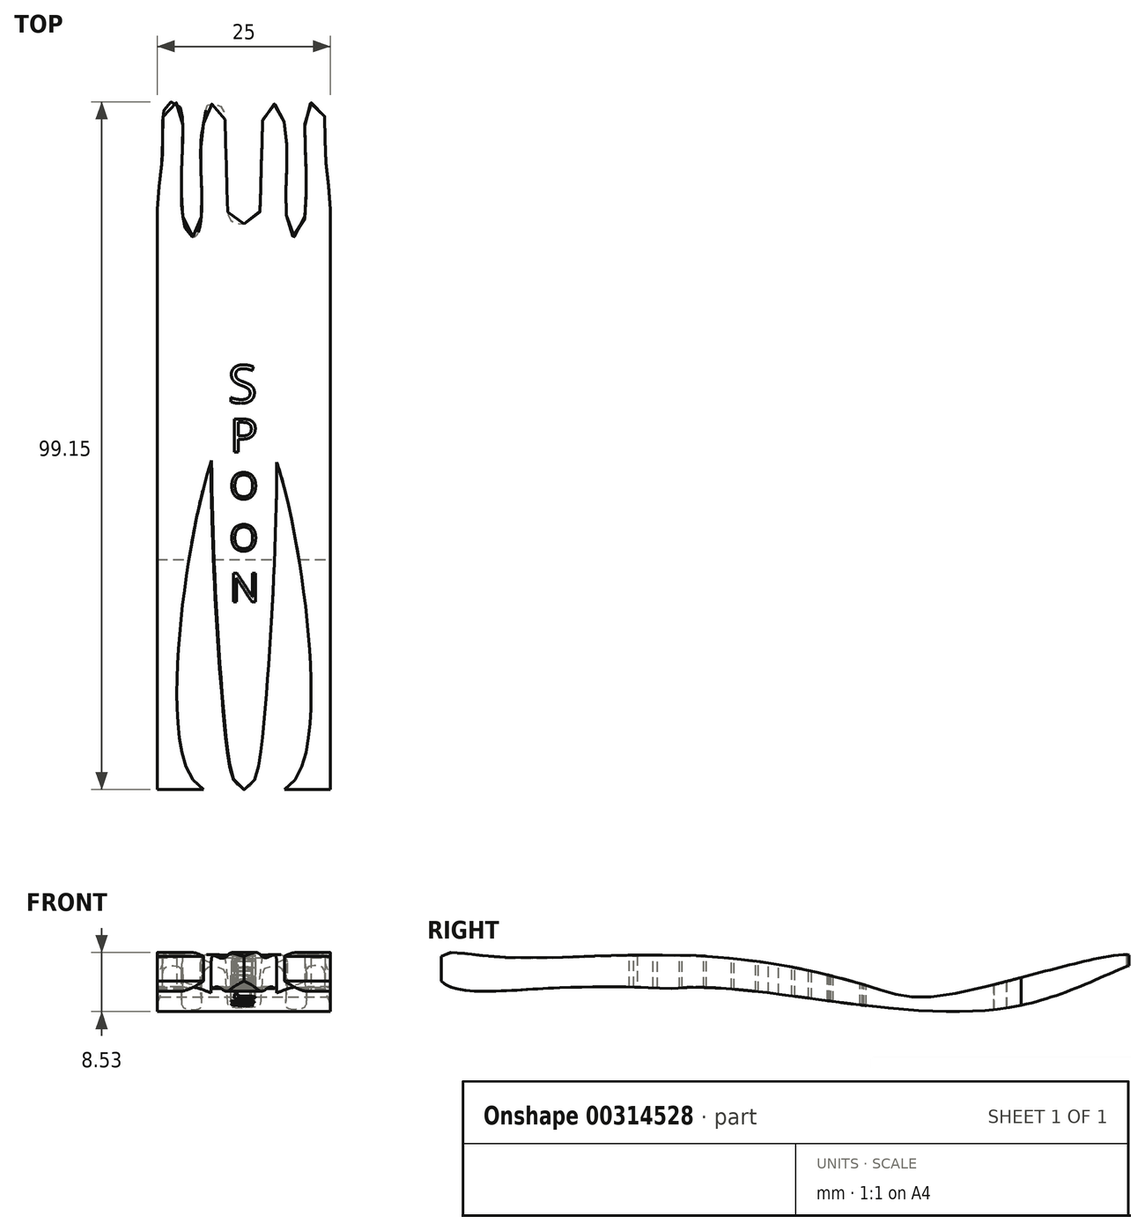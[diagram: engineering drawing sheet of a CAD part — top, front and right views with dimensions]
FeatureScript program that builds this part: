
annotation { "Feature Type Name" : "Feature", "Feature Type Description" : "" }
export const myFeature = defineFeature(function(context is Context, id is Id, definition is map)
    precondition{}
    {
        {
            var Q0;
            Q0=qCreatedBy(makeId("Top.planeOp"),FACE);
            var sketch = newSketch(context, id + "F0", { "sketchPlane" : qUnion([Q0])});
            skLineSegment(sketch, "E0.bottom", {"start": v(12.5, 50) * mm, "end": v(-12.5, 50) * mm});
            skLineSegment(sketch, "E0.top", {"start": v(12.5, -50) * mm, "end": v(-12.5, -50) * mm});
            skLineSegment(sketch, "E0.left", {"start": v(12.5, 50) * mm, "end": v(12.5, -50) * mm});
            skLineSegment(sketch, "E0.right", {"start": v(-12.5, 50) * mm, "end": v(-12.5, -50) * mm});
            skPoint(sketch, "E0.middle", {"position": v(0, 0) * mm});
            skSolve(sketch);
        }
        {
            var Q0;
            Q0=makeQuery(id+"F0.imprint","IMPRINT",FACE,{"disambiguationData":[TD([[makeQuery(id+"F0.imprint","IMPRINT",EDGE,{"derivedFrom":sQuery(id+"F0.wireOp",EDGE,"E0.bottom")}),1.0]])]});
            extrude(context, id + "F1", {"entities" : qUnion([Q0]), "depth" : 30 * mm});
        }
        {
            var Q0;
            Q0=makeQuery(id+"F1.opExtrude","CAP_FACE",FACE,{"disambiguationData":[OSD([sQuery(id+"F0.wireOp",EDGE,"E0.bottom"),sQuery(id+"F0.wireOp",EDGE,"E0.top"),sQuery(id+"F0.wireOp",EDGE,"E0.left"),sQuery(id+"F0.wireOp",EDGE,"E0.right")])],"isStart":false});
            var sketch = newSketch(context, id + "F2", { "sketchPlane" : qUnion([Q0])});
            skFitSpline(sketch, "E1.MirrorCS", {"points": [v(0, 31.54) * mm, v(-1.96, 32.06) * mm, v(-2.2, 32.35) * mm, v(-2.53, 40.64) * mm, v(-2.7, 45.52) * mm, v(-3.52, 48.65) * mm, v(-5.37, 48.65) * mm, v(-5.43, 48.53) * mm, v(-5.92, 45.53) * mm, v(-6.22, 40.95) * mm, v(-6.76, 29.96) * mm, v(-8.08, 30.17) * mm, v(-8.89, 41.38) * mm, v(-9.59, 48.9) * mm, v(-11.15, 48.73) * mm, v(-11.74, 41.56) * mm, v(-11.5, 27.74) * mm, v(-4.2, 21.83) * mm, v(-4.32, 9.89) * mm, v(-2.32, -45.14) * mm, v(0, -50) * mm, v(7.9, -47.77) * mm, v(3.4, 0.05) * mm, v(0.03, -49.28) * mm], "startDerivative": vector(-83.8, -22.38) * mm, "endDerivative": vector(1.6, -694.26) * mm});
            skLineSegment(sketch, "E2", {"start": v(0, 31.54) * mm, "end": v(0.03, -49.28) * mm});
            skFitSpline(sketch, "E3.MirrorCS", {"points": [v(0, 31.54) * mm, v(1.96, 32.06) * mm, v(2.2, 32.35) * mm, v(2.52, 40.65) * mm, v(2.69, 45.52) * mm, v(3.5, 48.65) * mm, v(5.35, 48.65) * mm, v(5.42, 48.53) * mm, v(5.91, 45.53) * mm, v(6.22, 40.95) * mm, v(6.77, 29.96) * mm, v(8.08, 30.17) * mm, v(8.88, 41.38) * mm, v(9.57, 48.9) * mm, v(11.14, 48.73) * mm, v(11.74, 41.57) * mm, v(11.5, 27.75) * mm, v(4.2, 21.83) * mm, v(4.33, 9.9) * mm, v(2.37, -45.14) * mm, v(0.05, -50) * mm, v(-7.84, -47.78) * mm, v(-3.37, 0.04) * mm, v(0.03, -49.28) * mm], "startDerivative": vector(83.82, -22.33) * mm, "endDerivative": vector(-1.16, -694.26) * mm});
            skSolve(sketch);
        }
        {
            var Q0;
            Q0=makeQuery(id+"F1.opExtrude","SWEPT_FACE",FACE,{"disambiguationData":[OSD([sQuery(id+"F0.wireOp",EDGE,"E0.left")])]});
            var sketch = newSketch(context, id + "F3", { "sketchPlane" : qUnion([Q0])});
            skLineSegment(sketch, "E4", {"start": v(0, 30) * mm, "end": v(0, 0) * mm, "construction": true});
            skLineSegment(sketch, "E5.bottom", {"start": v(50, 22.3) * mm, "end": v(-50, 22.3) * mm, "construction": true});
            skLineSegment(sketch, "E5.top", {"start": v(50, 7.7) * mm, "end": v(-50, 7.7) * mm, "construction": true});
            skLineSegment(sketch, "E5.left", {"start": v(50, 22.3) * mm, "end": v(50, 7.7) * mm, "construction": true});
            skLineSegment(sketch, "E5.right", {"start": v(-50, 22.3) * mm, "end": v(-50, 7.7) * mm, "construction": true});
            skPoint(sketch, "E5.middle", {"position": v(0, 15) * mm});
            skFitSpline(sketch, "E6", {"points": [v(50, 22.3) * mm, v(22.87, 16.73) * mm, v(12.16, 17.85) * mm, v(-11.49, 22.3) * mm, v(-43.17, 22.3) * mm, v(-50, 22.3) * mm, v(-50, 18.74) * mm, v(-36.03, 17.62) * mm, v(-12.83, 17.4) * mm, v(11.27, 14.05) * mm, v(22.42, 12.05) * mm, v(47.4, 18.3) * mm, v(50, 22.3) * mm]});
            skSolve(sketch);
        }
        {
            var Q0;
            {var subQ1=sQuery(id+"F0.wireOp",EDGE,"E0.left");var subQ6=makeQuery(id+"F1.opExtrude","CAP_EDGE",EDGE,{"disambiguationData":[OSD([subQ1])],"isStart":false});Q0=makeQuery(id+"F3.imprint","IMPRINT",FACE,{"disambiguationData":[TD([[makeQuery(id+"F3.imprint","IMPRINT",EDGE,{"derivedFrom":subQ6}),1.0]])]});}
            var Q1;
            {var subQ1=sQuery(id+"F0.wireOp",EDGE,"E0.left");var subQ6=makeQuery(id+"F1.opExtrude","CAP_EDGE",EDGE,{"disambiguationData":[OSD([subQ1])],"isStart":true});Q1=makeQuery(id+"F3.imprint","IMPRINT",FACE,{"disambiguationData":[TD([[makeQuery(id+"F3.imprint","IMPRINT",EDGE,{"derivedFrom":subQ6}),-1.0]])]});}
            extrude(context, id + "F4", {"entities" : qUnion([Q0, Q1]), "operationType" : NewBodyOperationType.REMOVE, "oppositeDirection" : true, "depth" : 30 * mm});
        }
        {
            var Q0;
            {var subQ0=sQuery(id+"F2.wireOp",EDGE,"E1.MirrorCS");var subQ1=makeQuery(id+"F1.opExtrude","CAP_EDGE",EDGE,{"disambiguationData":[OSD([sQuery(id+"F0.wireOp",EDGE,"E0.top")])],"isStart":false});var subQ2=makeQuery(id+"F2.imprint","INTERSECT",VERTEX,{"derivedFrom":[subQ1,subQ0]});Q0=makeQuery(id+"F2.imprint","IMPRINT",FACE,{"disambiguationData":[TD([[makeQuery(id+"F2.imprint","IMPRINT",EDGE,{"disambiguationData":[TD([[subQ2,1.0]])],"derivedFrom":subQ0}),-1.0]])]});}
            var Q1;
            {var subQ0=sQuery(id+"F2.wireOp",EDGE,"E3.MirrorCS");var subQ1=makeQuery(id+"F1.opExtrude","CAP_EDGE",EDGE,{"disambiguationData":[OSD([sQuery(id+"F0.wireOp",EDGE,"E0.top")])],"isStart":false});var subQ2=makeQuery(id+"F2.imprint","INTERSECT",VERTEX,{"derivedFrom":[subQ1,subQ0]});Q1=makeQuery(id+"F2.imprint","IMPRINT",FACE,{"disambiguationData":[TD([[makeQuery(id+"F2.imprint","IMPRINT",EDGE,{"disambiguationData":[TD([[subQ2,1.0]])],"derivedFrom":subQ0}),1.0]])]});}
            var Q2;
            {var subQ0=makeQuery(id+"F1.opExtrude","CAP_EDGE",EDGE,{"disambiguationData":[OSD([sQuery(id+"F0.wireOp",EDGE,"E0.bottom")])],"isStart":false});Q2=makeQuery(id+"F2.imprint","IMPRINT",FACE,{"disambiguationData":[TD([[makeQuery(id+"F2.imprint","IMPRINT",EDGE,{"derivedFrom":subQ0}),1.0]])]});}
            extrude(context, id + "F5", {"entities" : qUnion([Q0, Q1, Q2]), "operationType" : NewBodyOperationType.REMOVE, "oppositeDirection" : true, "depth" : 30 * mm});
        }
        {
            var Q0;
            Q0=qCreatedBy(makeId("Right.planeOp"),FACE);
            var sketch = newSketch(context, id + "F6", { "sketchPlane" : qUnion([Q0])});
            skFitSpline(sketch, "E7", {"points": [v(50.3, 21.42) * mm, v(35.14, 15.62) * mm, v(7.92, 15.62) * mm, v(-21.97, 15.4) * mm, v(7.7, -13.16) * mm, v(68.6, -10.26) * mm, v(58.11, 20.3) * mm, v(50.3, 21.42) * mm]});
            skSolve(sketch);
        }
        {
            var Q0;
            Q0 = qSketchRegion(id + "F6", true);
            extrude(context, id + "F7", {"entities" : qUnion([Q0]), "operationType" : NewBodyOperationType.REMOVE, "endBound" : BoundingType.SYMMETRIC, "oppositeDirection" : true, "depth" : 300 * mm});
        }
        {
            var Q0;
            {var subQ0=sQuery(id+"F2.wireOp",EDGE,"E1.MirrorCS");var subQ1=sQuery(id+"F0.wireOp",EDGE,"E0.right");Q0=makeQuery(id+"F5.boolean.opBoolean","COPY",EDGE,{"derivedFrom":makeQuery(id+"F5.opExtrude","SWEPT_EDGE",EDGE,{"disambiguationData":[OSD([subQ1,subQ0]),TDD([makeQuery(id+"F2.imprint","INTERSECT",VERTEX,{"disambiguationData":[OD(1.0)],"derivedFrom":[makeQuery(id+"F1.opExtrude","CAP_EDGE",EDGE,{"disambiguationData":[OSD([subQ1])],"isStart":false}),subQ0]})])]})});}
            var Q1;
            Q1=makeQuery(id+"F5.boolean.opBoolean","COPY",EDGE,{"derivedFrom":makeQuery(id+"F5.opExtrude","SWEPT_EDGE",EDGE,{"disambiguationData":[OSD([sQuery(id+"F0.wireOp",EDGE,"E0.top"),sQuery(id+"F2.wireOp",EDGE,"E1.MirrorCS")])]})});
            fillet(context, id + "F8", {"entities" : qUnion([Q0, Q1]), "radius" : 0.5 * mm, "tangentPropagation" : true, "allowEdgeOverflow" : false});
        }
        {
            var Q0;
            {var subQ0=sQuery(id+"F2.wireOp",EDGE,"E1.MirrorCS");var subQ1=sQuery(id+"F0.wireOp",EDGE,"E0.top");var subQ2=sQuery(id+"F3.wireOp",EDGE,"E6");var subQ3=sQuery(id+"F0.wireOp",EDGE,"E0.left");Q0=makeQuery(id+"F5.boolean.opBoolean","INTERSECT",EDGE,{"derivedFrom":[makeQuery(id+"F4.boolean.opBoolean","COPY",FACE,{"derivedFrom":makeQuery(id+"F4.opExtrude","SWEPT_FACE",FACE,{"disambiguationData":[OSD([subQ2]),TDD([makeQuery(id+"F3.imprint","IMPRINT",EDGE,{"disambiguationData":[TD([[makeQuery(id+"F3.imprint","INTERSECT",VERTEX,{"disambiguationData":[OD(0.0)],"derivedFrom":[makeQuery(id+"F1.opExtrude","SWEPT_EDGE",EDGE,{"disambiguationData":[OSD([subQ1,subQ3])]}),subQ2]}),1.0]])],"derivedFrom":subQ2})])]})}),makeQuery(id+"F5.opExtrude","SWEPT_FACE",FACE,{"disambiguationData":[OSD([subQ0]),TDD([makeQuery(id+"F2.imprint","IMPRINT",EDGE,{"disambiguationData":[TD([[makeQuery(id+"F2.imprint","INTERSECT",VERTEX,{"derivedFrom":[makeQuery(id+"F1.opExtrude","CAP_EDGE",EDGE,{"disambiguationData":[OSD([subQ1])],"isStart":false}),subQ0]}),1.0]])],"derivedFrom":subQ0})])]})]});}
            fillet(context, id + "F9", {"entities" : qUnion([Q0]), "radius" : .1 * mm, "tangentPropagation" : true, "allowEdgeOverflow" : false});
        }
        {
            var Q0;
            Q0=makeQuery(id+"F0.imprint","IMPRINT",FACE,{"disambiguationData":[TD([[makeQuery(id+"F0.imprint","IMPRINT",EDGE,{"derivedFrom":sQuery(id+"F0.wireOp",EDGE,"E0.bottom")}),1.0]])]});
            var sketch = newSketch(context, id + "F10", { "sketchPlane" : qUnion([Q0])});
            skText(sketch, "E8", { "text": "P", "fontName": "OpenSans-Regular.ttf"});
            skText(sketch, "E9", { "text": "O", "fontName": "OpenSans-Regular.ttf"});
            skText(sketch, "E10", { "text": "O", "fontName": "OpenSans-Regular.ttf"});
            skText(sketch, "E11", { "text": "N", "fontName": "OpenSans-Regular.ttf"});
            skText(sketch, "E12", { "text": "S", "fontName": "OpenSans-Regular.ttf"});
            const initialGuessF10  = {"E8": [-0.00204, -0.00138, 1, 0, 0.00483], "E9": [-0.00207, -0.00811, 1, 0, 0.0038], "E10": [-0.00207, -0.01561, 1, 0, 0.0038], "E11": [-0.00207, -0.02293, 1, 0, 0.00413], "E12": [-0.00227, 0.00573, 1, 0, 0.00547]};
            skSetInitialGuess(sketch, initialGuessF10);
            skSolve(sketch);
        }
        {
            var Q0;
            Q0 = qSketchRegion(id + "F10", true);
            extrude(context, id + "F11", {"entities" : qUnion([Q0]), "operationType" : NewBodyOperationType.REMOVE, "endBound" : BoundingType.SYMMETRIC, "oppositeDirection" : true, "depth" : 100 * mm});
        }
    });
